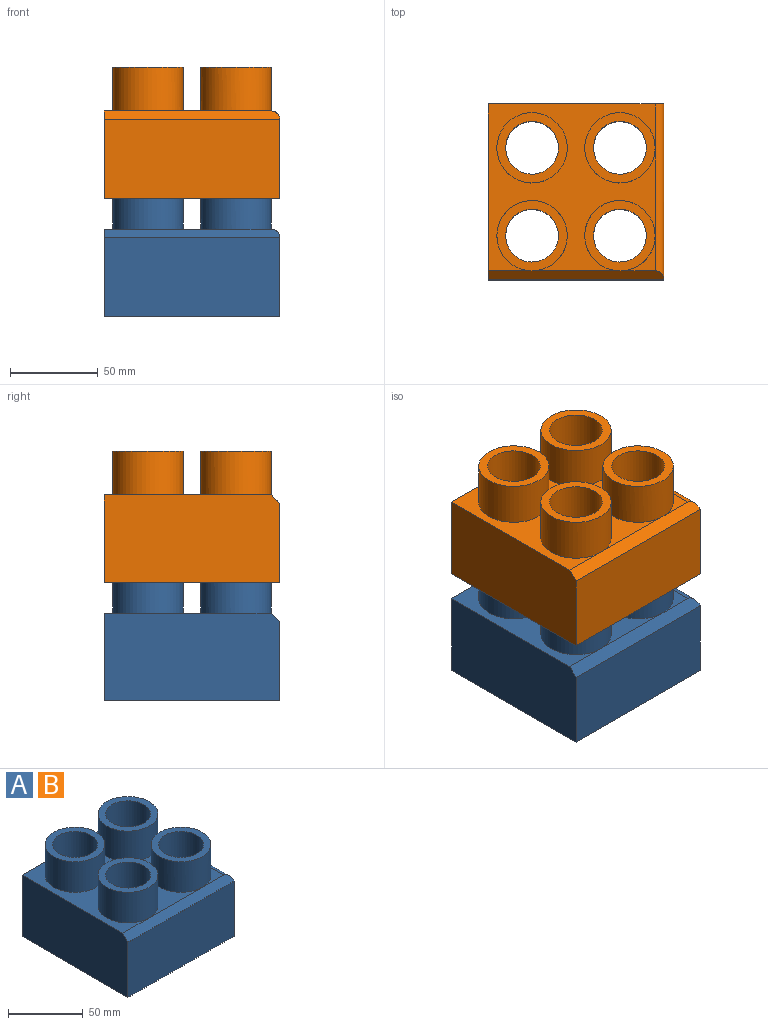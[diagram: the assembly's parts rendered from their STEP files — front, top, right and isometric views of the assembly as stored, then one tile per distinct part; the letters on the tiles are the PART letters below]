
ASSEMBLY  parts=2 mates=1
PART A: 29 faces, bbox 100x100x75 mm
  f0: plane 20x20mm, normal (0,0,1), area 85.8mm2, adj f24,f27,f28
  f1: cylinder r=20mm len=45mm, axis (0,0,1), area 5654.9mm2, adj f9,f26
  f2: cylinder r=20mm len=45mm, axis (0,0,1), area 5654.9mm2, adj f9,f22
  f3: cylinder r=20mm len=45mm, axis (0,0,1), area 5654.9mm2, adj f9,f18
  f4: cylinder r=20mm len=45mm, axis (0,0,1), area 5654.9mm2, adj f9,f14
  f5: plane 100x50mm, normal (0,1,0), area 4994.6mm2, adj f6,f8,f9,f10,f28
  f6: plane 100x50mm, normal (-1,0,0), area 4987.5mm2, adj f5,f7,f9,f10,f27
  f7: plane 100x45mm, normal (0,-1,0), area 4500mm2, adj f6,f8,f9,f27
  f8: plane 100x45mm, normal (1,0,0), area 4500mm2, adj f5,f7,f9,f28
  f9: plane 100x100mm, normal (0,0,-1), area 4973.5mm2, adj f1,f2,f3,f4,f5,f6,f7,f8
  f10: plane 95x95mm, normal (0,0,1), area 3912.6mm2, adj f5,f6,f12,f16,f20,f24,f27,f28
  f11: cylinder r=15mm len=30mm, axis (0,0,-1), area 2827.4mm2, adj f13,f14
  f12: cylinder r=20mm len=40mm, axis (0,0,-1), area 3141.6mm2, adj f10,f13
  f13: plane 40x40mm, normal (0,0,1), area 549.8mm2, adj f11,f12
  f14: plane 40x40mm, normal (0,0,-1), area 549.8mm2, adj f4,f11
  f15: cylinder r=15mm len=30mm, axis (0,0,-1), area 2827.4mm2, adj f17,f18
  f16: cylinder r=20mm len=40mm, axis (0,0,-1), area 3141.6mm2, adj f10,f17
  f17: plane 40x40mm, normal (0,0,1), area 549.8mm2, adj f15,f16
  f18: plane 40x40mm, normal (0,0,-1), area 549.8mm2, adj f3,f15
  f19: cylinder r=15mm len=30mm, axis (0,0,-1), area 2827.4mm2, adj f21,f22
  f20: cylinder r=20mm len=40mm, axis (0,0,-1), area 3141.6mm2, adj f10,f21
  f21: plane 40x40mm, normal (0,0,1), area 549.8mm2, adj f19,f20
  f22: plane 40x40mm, normal (0,0,-1), area 549.8mm2, adj f2,f19
  f23: cylinder r=15mm len=30mm, axis (0,0,-1), area 2827.4mm2, adj f25,f26
  f24: cylinder r=20mm len=40mm, axis (0,0,-1), area 3141.6mm2, adj f0,f10,f25
  f25: plane 40x40mm, normal (0,0,1), area 549.8mm2, adj f23,f24
  f26: plane 40x40mm, normal (0,0,-1), area 549.8mm2, adj f1,f23
  f27: plane 100x5mm, normal (0,-0.71,0.71), area 699.5mm2, adj f0,f6,f7,f10,f28
  f28: cylinder r=5mm len=100mm, axis (0,1,0), area 760.4mm2, adj f0,f5,f8,f10,f27
PART B: same geometry as A
PLACE A t=(56.21,37.95,5.89)mm
PLACE B t=(56.21,37.95,73.13)mm
MATE slider B.f1 <-> A.f1  axis (0,0,1) through (81.21,12.95,23.13)mm
